# Revit family: ASSA_ABLOY_DockLeveler_DL6220TA
name_source: partatom
category: Mechanical Equipment
units: mm (PartAtom-declared; Revit-internal decimal feet)

## family parameters
Always vertical = Yes
Classification = None
Cut with Voids When Loaded = No
Part Type = Normal
Room Calculation Point = No
Round Connector Dimension = Use Diameter
Shared = No
Work Plane-Based = No

## types (3) — shared parameters
DL6220T_LipLL1000 = DL6220T_Platform : DL6220T_LipLL1000
DL6220T_LipLL500 = DL6220T_Platform : DL6220T_LipLL500
Description = Dock Leveler
Manufacturer = ASSA ABLOY
Model = DL6220TA
VoidCutterRetracingLip500 = 200 mm  [stored 0.656168 ft]
VoidRetracingLip500Height = 2 mm  [stored 0.00656168 ft]

## per-type parameters (varying)
| type | LipLength | LipType |
| Lip LL1000 | 500 mm  [stored 1.64042 ft] | DL6220T_Platform : DL6220T_LipLL500 |
| Lip LL500 | 500 mm  [stored 1.64042 ft] | DL6220T_Platform : DL6220T_LipLL500 |
| LipErgo LL345 | 345 mm  [stored 1.13189 ft] | DL6220T_ErgoPlatform : DL6220TE_LipErgoLL345 |

note: [stored X ft] marks values corroborated as IEEE doubles in the binary element streams (Revit-internal decimal feet)

## geometry (parser evidence)
native form markers: Sweep x27
no freeform markers — native parametric forms only
